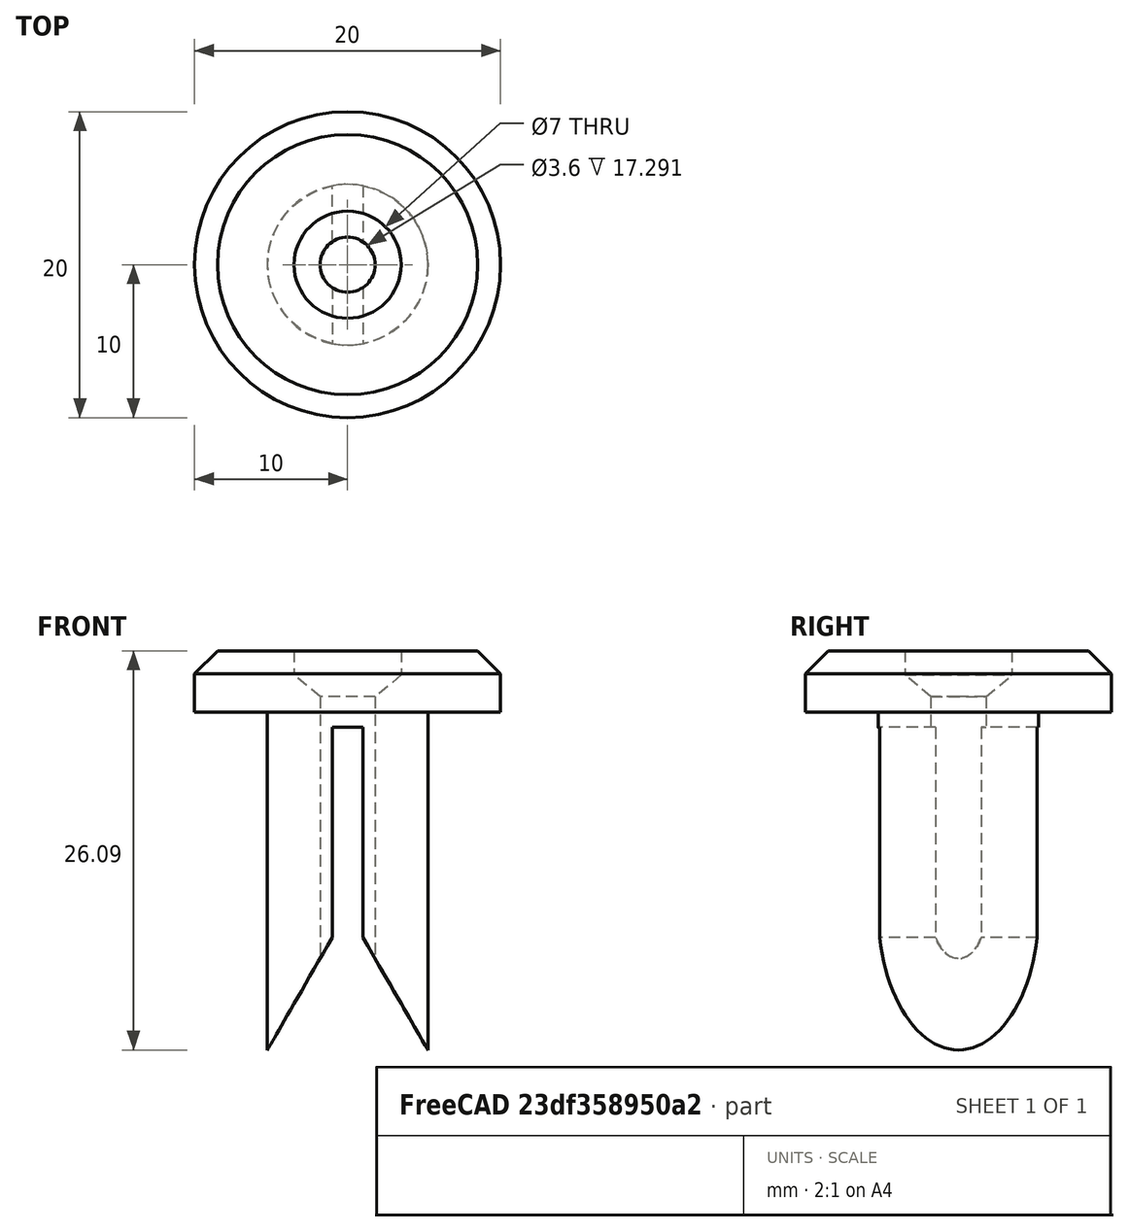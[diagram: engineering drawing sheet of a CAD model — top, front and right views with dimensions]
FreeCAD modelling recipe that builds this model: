
FCSTD DOCUMENT  (FreeCAD 0.16R)
Label: Barends
License: All rights reserved
LicenseURL: http://en.wikipedia.org/wiki/All_rights_reserved
objects: Sketcher::SketchObject×3, Part::Cut×3, PartDesign::Pad×2, PartDesign::Revolution×1, Mesh::Feature×1
note: 12 computed .brp shape members not serialized (recipe doc carries the construction recipe); baked Part::Feature solids carry a one-line shape summary decoded from their .brp

FEATURE [Sketcher::SketchObject] Sketch
  Placement = pos=(0,0,0) rot=(1,0,0;1.5708rad)
  sketch-geometry (9):
    g0: LineSegment StartX=3.5 StartY=4 StartZ=0 EndX=8.5 EndY=4 EndZ=0
    g1: LineSegment StartX=8.5 StartY=4 StartZ=0 EndX=10 EndY=2.5 EndZ=0
    g2: LineSegment StartX=10 StartY=2.5 StartZ=0 EndX=10 EndY=0 EndZ=0
    g3: LineSegment StartX=10 StartY=0 StartZ=0 EndX=5.25 EndY=0 EndZ=0
    g4: LineSegment StartX=5.25 StartY=0 StartZ=0 EndX=5.25 EndY=-23 EndZ=0
    g5: LineSegment StartX=5.25 StartY=-23 StartZ=0 EndX=1.8 EndY=-23 EndZ=0
    g6: LineSegment StartX=3.5 StartY=4 StartZ=0 EndX=3.5 EndY=2.42647 EndZ=0
    g7: LineSegment StartX=3.5 StartY=2.42647 StartZ=0 EndX=1.8 EndY=1 EndZ=0
    g8: LineSegment StartX=1.8 StartY=1 StartZ=0 EndX=1.8 EndY=-23 EndZ=0
  constraints (27):
    c: Horizontal(g0)
    c: Coincident(g0,g1)
    c: Coincident(g1,g2)
    c: Coincident(g2,g3)
    c: Coincident(g3,g4)
    c: Vertical(g4)
    c: Coincident(g4,g5)
    c: Horizontal(g5)
    c: Vertical(g6)
    c: Coincident(g6,g7)
    c: Coincident(g7,g8)
    c: Coincident(g0,g6)
    c: Horizontal(g3)
    c: Coincident(g8,g5)
    c: Vertical(g8)
    c: DistanceX(g-1,g0) = 3.5
    c: DistanceX(g-1,g7) = 1.8
    c: DistanceX(g-1,g3) = 5.25
    c: DistanceX(g-1,g2) = 10
    c: Vertical(g2)
    c: PointOnObject(g3,g-1)
    c: Distance(g8) = 24
    c: DistanceY(g4,g4) = 23
    c: DistanceY(g2,g2) = 2.5
    c: DistanceY(g0) = 4
    c: Angle(g1) = -0.785398
    c: Angle(g7) = 3.83972
FEATURE [PartDesign::Revolution] Revolution
  Angle = 360
  Axis = (0,0,1)
  Base = (0,0,0)
  Placement = pos=(0,0,0) rot=(1,0,0;1.5708rad)
  ReferenceAxis = -> Sketch [V_Axis]
  Reversed = true
  Sketch = -> Sketch
FEATURE [Sketcher::SketchObject] Sketch001
  Placement = pos=(0,0,0) rot=(1,0,0;1.5708rad)
  sketch-geometry (4):
    g0: LineSegment StartX=8 StartY=-26.8564 StartZ=0 EndX=0 EndY=-13 EndZ=0
    g1: LineSegment StartX=0 StartY=-13 StartZ=0 EndX=-8 EndY=-26.8564 EndZ=0
    g2: LineSegment StartX=-8 StartY=-26.8564 StartZ=0 EndX=8 EndY=-26.8564 EndZ=0
    g3: Circle [constr] CenterX=0 CenterY=-22.2376 CenterZ=0 NormalX=0 NormalY=0 NormalZ=1 Radius=9.2376
  constraints (12):
    c: Coincident(g0,g1)
    c: Coincident(g1,g2)
    c: Coincident(g2,g0)
    c: Equal(g0,g1)
    c: Equal(g0,g2)
    c: PointOnObject(g0,g3)
    c: PointOnObject(g1,g3)
    c: PointOnObject(g2,g3)
    c: Horizontal(g2)
    c: PointOnObject(g0,g-2)
    c: Distance(g1) = 16
    c: DistanceY(g0,g-1) = 13
FEATURE [PartDesign::Pad] Pad
  Length = 15
  Length2 = 100
  Midplane = true
  Placement = pos=(0,0,0) rot=(1,0,0;1.5708rad)
  Sketch = -> Sketch001
  Type = 0
FEATURE [Part::Cut] Cut
  Base = -> Revolution
  Tool = -> Pad
FEATURE [Sketcher::SketchObject] Sketch002
  Placement = pos=(0,0,0) rot=(1,0,0;1.5708rad)
  sketch-geometry (4):
    g0: LineSegment StartX=-1 StartY=-1 StartZ=0 EndX=1 EndY=-1 EndZ=0
    g1: LineSegment StartX=1 StartY=-1 StartZ=0 EndX=1 EndY=-26 EndZ=0
    g2: LineSegment StartX=1 StartY=-26 StartZ=0 EndX=-1 EndY=-26 EndZ=0
    g3: LineSegment StartX=-1 StartY=-26 StartZ=0 EndX=-1 EndY=-1 EndZ=0
  constraints (12):
    c: Coincident(g0,g1)
    c: Coincident(g1,g2)
    c: Coincident(g2,g3)
    c: Coincident(g3,g0)
    c: Horizontal(g0)
    c: Horizontal(g2)
    c: Vertical(g1)
    c: Vertical(g3)
    c: Symmetric(g2,g1,g-2)
    c: DistanceX(g2,g2) = 2
    c: DistanceY(g0) = -1
    c: Distance(g1) = 25
FEATURE [PartDesign::Pad] Pad001
  Length = 30
  Length2 = 100
  Midplane = true
  Placement = pos=(0,0,0) rot=(1,0,0;1.5708rad)
  Sketch = -> Sketch002
  Type = 0
FEATURE [Part::Cut] Cut001
  Base = -> Cut
  Tool = -> Pad001
FEATURE [Part::Cut] Cut002
  Base = -> Cut
  Tool = -> Pad001
FEATURE [Mesh::Feature] Mesh  label="Cut002 (Meshed)"
